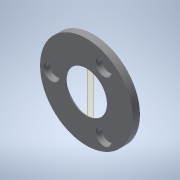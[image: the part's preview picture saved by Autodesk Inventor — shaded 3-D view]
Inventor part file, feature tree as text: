
AUTODESK INVENTOR PART (.ipt)
format: ipt  version: 2022 (Build 260153000, 153)  size: 182,272 bytes
history: native  units: mm
features: other x4, sketch x3, extrude x2, chamfer x2, reference x2, plane x1, revolve x1, projected_geometry x1
ambient origin geometry x8: Origin, YZ Plane, XZ Plane, XY Plane, X Axis, Y Axis, Z Axis, Center Point
bodies: Volumenkörper1 (feature_tree)
feature tree (16):
  plane  "Arbeitsebene1"
  revolve  "Umdrehung1"
  extrude  "Extrusion1"  Depth=3.1mm
  chamfer  "Fase1"  [1 undecoded]
  extrude  "Extrusion2"  Depth=1.0mm
  chamfer  "Fase2"  Distance=0.25mm
  sketch  "Skizze1"  dims[d0=0.4mm d1=3.1mm]
  reference  "Referenz1"
  reference  "Referenz2"
  sketch  "Skizze2"  dims[d2=9.0mm]
  projected_geometry  "Projizierte Kontur1"
  sketch  "Skizze3"  dims[d3=0.6mm d4=0.0mm d5=1.0mm d6=0.25mm d7=90.0deg d8=47.984381mm d9=29.984381mm d10=19.49219mm d11=8.0mm d12=8.0mm d13=8.0mm d14=3.0mm d15=0.0mm d16=0.5mm d17=2.0mm d18=45.0deg d19=52.0mm d20=4.0mm d21=0.0mm d22=0.6mm d23=2.0mm d24=45.0deg]
  other  "SMLM_Holder_v1.iam"
  other  "00_Coverglass_25mm:1"
  other  "Baugruppe1"
  other  "01_SMLM_Holder_Base:1"
note: 1 required parameter value undecoded (feature->parameter linkage not recoverable at this tier; creation-order binding heuristic only, values carry confidence <= 0.55)
